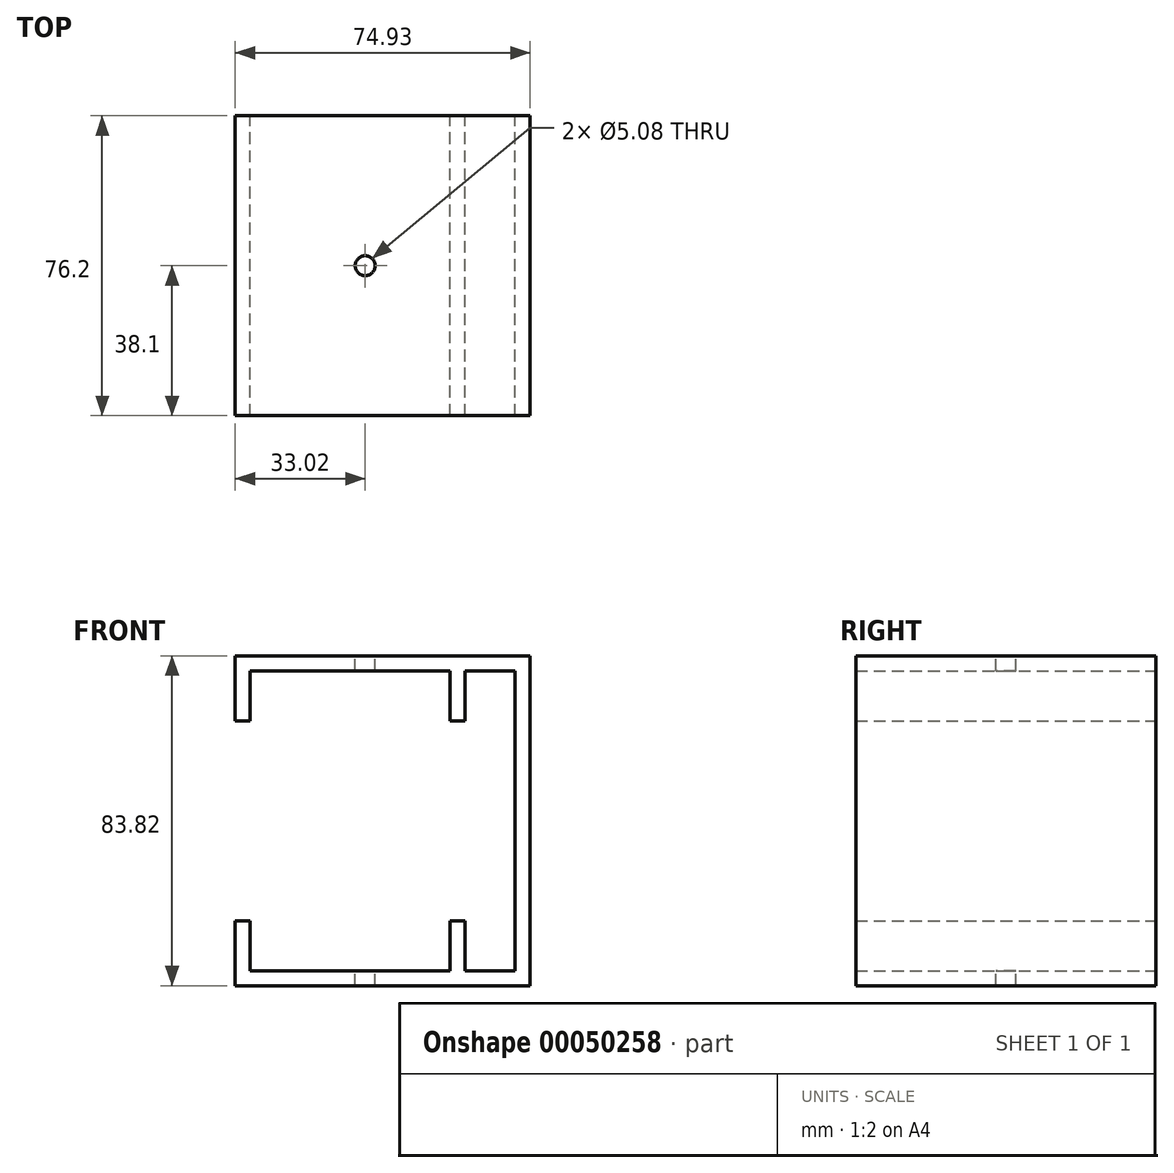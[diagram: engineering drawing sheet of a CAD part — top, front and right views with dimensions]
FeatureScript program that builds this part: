
annotation { "Feature Type Name" : "Feature", "Feature Type Description" : "" }
export const myFeature = defineFeature(function(context is Context, id is Id, definition is map)
    precondition{}
    {
        {
            var Q0;
            Q0=qCreatedBy(makeId("Front.planeOp"),FACE);
            var sketch = newSketch(context, id + "F0", { "sketchPlane" : qUnion([Q0])});
            skLineSegment(sketch, "E0", {"start": v(54.61, 3.8) * mm, "end": v(54.61, 16.5) * mm});
            skLineSegment(sketch, "E1", {"start": v(0, 0) * mm, "end": v(0, 16.5) * mm});
            skLineSegment(sketch, "E2", {"start": v(58.42, 3.8) * mm, "end": v(58.42, 16.5) * mm});
            skLineSegment(sketch, "E3", {"start": v(0, 83.82) * mm, "end": v(0, 67.3) * mm});
            skLineSegment(sketch, "E4", {"start": v(0, 67.3) * mm, "end": v(3.8, 67.3) * mm});
            skLineSegment(sketch, "E5", {"start": v(3.8, 67.3) * mm, "end": v(3.8, 80) * mm});
            skLineSegment(sketch, "E6", {"start": v(54.61, 67.3) * mm, "end": v(58.42, 67.3) * mm});
            skLineSegment(sketch, "E7", {"start": v(54.61, 16.5) * mm, "end": v(58.42, 16.5) * mm});
            skLineSegment(sketch, "E8.trimOffspring", {"start": v(54.61, 67.3) * mm, "end": v(54.61, 80) * mm});
            skLineSegment(sketch, "E9.trimOffspring", {"start": v(58.42, 67.3) * mm, "end": v(58.42, 80) * mm});
            skLineSegment(sketch, "E10", {"start": v(71.12, 80) * mm, "end": v(71.12, 3.81) * mm});
            skLineSegment(sketch, "E11", {"start": v(74.93, 83.82) * mm, "end": v(74.93, 0) * mm});
            skLineSegment(sketch, "E12", {"start": v(58.42, 3.8) * mm, "end": v(71.12, 3.8) * mm});
            skLineSegment(sketch, "E13", {"start": v(3.81, 80) * mm, "end": v(54.61, 80) * mm});
            skLineSegment(sketch, "E14", {"start": v(0, 0) * mm, "end": v(74.93, 0) * mm});
            skLineSegment(sketch, "E15", {"start": v(74.93, 83.82) * mm, "end": v(0, 83.82) * mm});
            skLineSegment(sketch, "E16", {"start": v(0, 16.5) * mm, "end": v(3.8, 16.5) * mm});
            skLineSegment(sketch, "E17", {"start": v(3.8, 16.5) * mm, "end": v(3.81, 3.8) * mm});
            skLineSegment(sketch, "E18", {"start": v(3.8, 3.8) * mm, "end": v(54.61, 3.8) * mm});
            skLineSegment(sketch, "E19.trimOffspring", {"start": v(58.42, 80) * mm, "end": v(71.12, 80) * mm});
            skSolve(sketch);
        }
        {
            var Q0;
            Q0 = qSketchRegion(id + "F0", true);
            extrude(context, id + "F1", {"entities" : qUnion([Q0]), "depth" : 76.2 * mm});
        }
        {
            var Q0;
            Q0=makeQuery(id+"F1.opExtrude","SWEPT_FACE",FACE,{"disambiguationData":[OSD([sQuery(id+"F0.wireOp",EDGE,"E15")])]});
            var sketch = newSketch(context, id + "F2", { "sketchPlane" : qUnion([Q0])});
            skLineSegment(sketch, "E20", {"start": v(0, -38.1) * mm, "end": v(33.02, -38.1) * mm});
            skCircle(sketch, "E21", {"center": v(33.02, -38.1) * mm, "radius": 2.54 * mm});
            skSolve(sketch);
        }
        {
            var Q0;
            Q0 = qSketchRegion(id + "F2", true);
            extrude(context, id + "F3", {"entities" : qUnion([Q0]), "operationType" : NewBodyOperationType.REMOVE, "oppositeDirection" : true, "depth" : 101.6 * mm});
        }
    });
